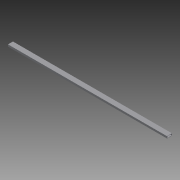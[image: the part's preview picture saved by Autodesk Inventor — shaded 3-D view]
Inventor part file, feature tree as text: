
AUTODESK INVENTOR PART (.ipt)
format: ipt  version: 2013 (Build 170138000, 138)  size: 78,336 bytes
history: native  units: in
note: dims shown in document units (in); Inventor stores cm internally (conversion verified against a paired STEP export)
features: other x2, extrude x1, sketch x1
ambient origin geometry x8: Origin, YZ Plane, XZ Plane, XY Plane, X Axis, Y Axis, Z Axis, Center Point
bodies: Solid1 (feature_tree)
feature tree (4):
  other  "Table"
  other  "squareTube_1x2-01"
  extrude  "Extrusion1"  Depth=2.5in
  sketch  "Sketch1"  dims[d0=1.0in d1=2.5in d2=0.125in d4=0.0in]
